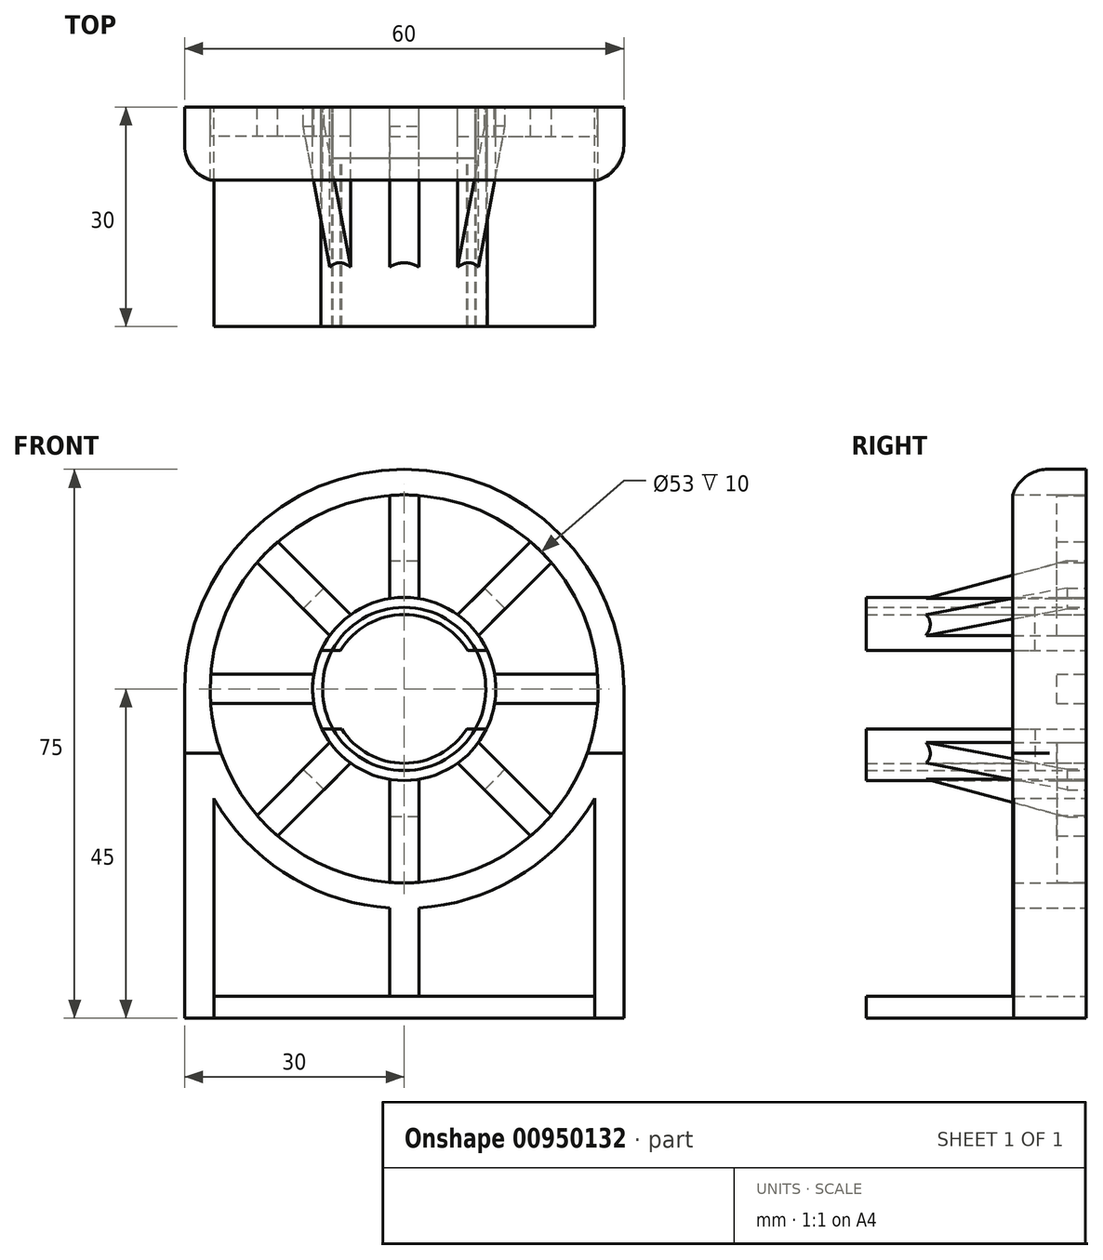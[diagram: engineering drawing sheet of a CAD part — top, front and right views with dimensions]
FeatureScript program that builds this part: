
annotation { "Feature Type Name" : "Feature", "Feature Type Description" : "" }
export const myFeature = defineFeature(function(context is Context, id is Id, definition is map)
    precondition{}
    {
        {
            var Q0;
            Q0=qCreatedBy(makeId("Front.planeOp"),FACE);
            var sketch = newSketch(context, id + "F0", { "sketchPlane" : qUnion([Q0])});
            skCircle(sketch, "E0", {"center": v(0, 0) * mm, "radius": 11.15 * mm});
            skCircle(sketch, "E1", {"center": v(0, 0) * mm, "radius": 10.15 * mm});
            skLineSegment(sketch, "E2.bottom", {"start": v(6.25, 8) * mm, "end": v(-6.25, 8) * mm});
            skLineSegment(sketch, "E2.top", {"start": v(6.25, -8) * mm, "end": v(-6.25, -8) * mm});
            skLineSegment(sketch, "E2.left", {"start": v(6.25, 8) * mm, "end": v(6.25, -8) * mm});
            skLineSegment(sketch, "E2.right", {"start": v(-6.25, 8) * mm, "end": v(-6.25, -8) * mm});
            skCircle(sketch, "E3", {"center": v(0, 0) * mm, "radius": 30 * mm});
            skCircle(sketch, "E4", {"center": v(0, 0) * mm, "radius": 26.5 * mm});
            skLineSegment(sketch, "E5", {"start": v(-30, 0) * mm, "end": v(-30, -45) * mm});
            skLineSegment(sketch, "E6", {"start": v(30, 0) * mm, "end": v(30, -45) * mm});
            skLineSegment(sketch, "E7", {"start": v(-30, -45) * mm, "end": v(30, -45) * mm});
            skLineSegment(sketch, "E8", {"start": v(-26, -45) * mm, "end": v(-26, -14.97) * mm});
            skLineSegment(sketch, "E9", {"start": v(26, -45) * mm, "end": v(26, -14.97) * mm});
            skLineSegment(sketch, "E10", {"start": v(-26, -42) * mm, "end": v(26, -42) * mm});
            skLineSegment(sketch, "E11", {"start": v(-2, -29.93) * mm, "end": v(-2, -42) * mm});
            skLineSegment(sketch, "E12", {"start": v(2, -29.93) * mm, "end": v(2, -42) * mm});
            skLineSegment(sketch, "E13", {"start": v(-8.7, 5.24) * mm, "end": v(-6.25, 5.24) * mm});
            skLineSegment(sketch, "E14", {"start": v(-6.25, 5.24) * mm, "end": v(6.25, 5.24) * mm});
            skLineSegment(sketch, "E15", {"start": v(6.25, 5.24) * mm, "end": v(8.7, 5.24) * mm});
            skLineSegment(sketch, "E16", {"start": v(8.54, -5.48) * mm, "end": v(6.25, -5.48) * mm});
            skLineSegment(sketch, "E17", {"start": v(6.25, -5.48) * mm, "end": v(-6.25, -5.48) * mm});
            skLineSegment(sketch, "E18", {"start": v(-6.25, -5.48) * mm, "end": v(-8.54, -5.48) * mm});
            skLineSegment(sketch, "E19", {"start": v(-8.7, 5.24) * mm, "end": v(-9.84, 5.24) * mm});
            skLineSegment(sketch, "E20", {"start": v(-8.54, -5.48) * mm, "end": v(-9.71, -5.48) * mm});
            skPoint(sketch, "E20.endSnap0", {"position": v(-7.4, -5.48) * mm});
            skLineSegment(sketch, "E21", {"start": v(8.54, -5.48) * mm, "end": v(9.71, -5.48) * mm});
            skLineSegment(sketch, "E22", {"start": v(8.7, 5.24) * mm, "end": v(9.84, 5.24) * mm});
            skCircle(sketch, "E23", {"center": v(0, 0) * mm, "radius": 12.5 * mm});
            skLineSegment(sketch, "E24", {"start": v(-12.34, 2) * mm, "end": v(-26.42, 2) * mm});
            skLineSegment(sketch, "E25", {"start": v(-12.34, -2) * mm, "end": v(-26.42, -2) * mm});
            skLineSegment(sketch, "E26.MirrorCS", {"start": v(12.34, 2) * mm, "end": v(26.42, 2) * mm});
            skLineSegment(sketch, "E27.MirrorCS", {"start": v(12.34, -2) * mm, "end": v(26.42, -2) * mm});
            skLineSegment(sketch, "E28", {"start": v(-2, 12.34) * mm, "end": v(-2, 26.42) * mm});
            skLineSegment(sketch, "E29", {"start": v(-2, -12.34) * mm, "end": v(-2, -26.42) * mm});
            skLineSegment(sketch, "E30.MirrorCS", {"start": v(2, 12.34) * mm, "end": v(2, 26.42) * mm});
            skLineSegment(sketch, "E31.MirrorCS", {"start": v(2, -12.34) * mm, "end": v(2, -26.42) * mm});
            skLineSegment(sketch, "E32", {"start": v(0, 0) * mm, "end": v(-18.74, 18.74) * mm});
            skLineSegment(sketch, "E33.MirrorCS", {"start": v(0, 0) * mm, "end": v(18.74, 18.74) * mm});
            skLineSegment(sketch, "E34.MirrorCS", {"start": v(0, 0) * mm, "end": v(18.74, -18.74) * mm});
            skLineSegment(sketch, "E35.MirrorCS", {"start": v(0, 0) * mm, "end": v(-18.74, -18.74) * mm});
            skLineSegment(sketch, "E36", {"start": v(-10.14, 7.31) * mm, "end": v(-20.1, 17.27) * mm});
            skLineSegment(sketch, "E37.MirrorCS", {"start": v(-7.31, 10.14) * mm, "end": v(-17.27, 20.1) * mm});
            skLineSegment(sketch, "E38.MirrorCS", {"start": v(7.31, -10.14) * mm, "end": v(17.27, -20.1) * mm});
            skLineSegment(sketch, "E39.MirrorCS", {"start": v(10.14, -7.31) * mm, "end": v(20.1, -17.27) * mm});
            skLineSegment(sketch, "E40.MirrorCS", {"start": v(10.14, 7.31) * mm, "end": v(20.1, 17.27) * mm});
            skLineSegment(sketch, "E41.MirrorCS", {"start": v(7.31, 10.14) * mm, "end": v(17.27, 20.1) * mm});
            skLineSegment(sketch, "E42.MirrorCS", {"start": v(-10.14, -7.31) * mm, "end": v(-20.1, -17.27) * mm});
            skLineSegment(sketch, "E43.MirrorCS", {"start": v(-7.31, -10.14) * mm, "end": v(-17.27, -20.1) * mm});
            skLineSegment(sketch, "E44", {"start": v(-9.84, 5.24) * mm, "end": v(-11.35, 5.24) * mm});
            skLineSegment(sketch, "E45", {"start": v(9.84, 5.24) * mm, "end": v(11.35, 5.24) * mm});
            skLineSegment(sketch, "E46", {"start": v(9.71, -5.48) * mm, "end": v(11.24, -5.48) * mm});
            skLineSegment(sketch, "E47", {"start": v(-9.71, -5.48) * mm, "end": v(-11.24, -5.48) * mm});
            skLineSegment(sketch, "E48", {"start": v(-10.96, 13.79) * mm, "end": v(-13.79, 10.96) * mm});
            skLineSegment(sketch, "E49.MirrorCS", {"start": v(10.96, 13.79) * mm, "end": v(13.79, 10.96) * mm});
            skLineSegment(sketch, "E50.MirrorCS", {"start": v(10.96, -13.79) * mm, "end": v(13.79, -10.96) * mm});
            skLineSegment(sketch, "E51.MirrorCS", {"start": v(-10.96, -13.79) * mm, "end": v(-13.79, -10.96) * mm});
            skLineSegment(sketch, "E52", {"start": v(-2, -17.5) * mm, "end": v(2, -17.5) * mm});
            skLineSegment(sketch, "E53.MirrorCS", {"start": v(-2, 17.5) * mm, "end": v(2, 17.5) * mm});
            skLineSegment(sketch, "E54.MirrorCS", {"start": v(17.5, -2) * mm, "end": v(17.5, 2) * mm});
            skLineSegment(sketch, "E55.MirrorCS", {"start": v(-17.5, 2) * mm, "end": v(-17.5, -2) * mm});
            skCircle(sketch, "E56", {"center": v(0, 0) * mm, "radius": 8.5 * mm});
            skSolve(sketch);
        }
        {
            var Q0;
            {var subQ0=sQuery(id+"F0.wireOp",EDGE,"E19");Q0=makeQuery(id+"F0.imprint","IMPRINT",FACE,{"disambiguationData":[TD([[makeQuery(id+"F0.imprint","IMPRINT",EDGE,{"derivedFrom":subQ0}),-1.0]])]});}
            var Q1;
            {var subQ4=sQuery(id+"F0.wireOp",EDGE,"E33.MirrorCS");var subQ8=sQuery(id+"F0.wireOp",EDGE,"E0");var subQ9=makeQuery(id+"F0.imprint","INTERSECT",VERTEX,{"derivedFrom":[subQ8,subQ4]});Q1=makeQuery(id+"F0.imprint","IMPRINT",FACE,{"disambiguationData":[TD([[makeQuery(id+"F0.imprint","IMPRINT",EDGE,{"disambiguationData":[TD([[subQ9,-1.0]])],"derivedFrom":subQ8}),1.0]])]});}
            var Q2;
            {var subQ0=sQuery(id+"F0.wireOp",EDGE,"E22");Q2=makeQuery(id+"F0.imprint","IMPRINT",FACE,{"disambiguationData":[TD([[makeQuery(id+"F0.imprint","IMPRINT",EDGE,{"derivedFrom":subQ0}),1.0]])]});}
            var Q3;
            {var subQ0=sQuery(id+"F0.wireOp",EDGE,"E21");Q3=makeQuery(id+"F0.imprint","IMPRINT",FACE,{"disambiguationData":[TD([[makeQuery(id+"F0.imprint","IMPRINT",EDGE,{"derivedFrom":subQ0}),-1.0]])]});}
            var Q4;
            {var subQ6=sQuery(id+"F0.wireOp",EDGE,"E35.MirrorCS");var subQ7=sQuery(id+"F0.wireOp",EDGE,"E0");var subQ8=makeQuery(id+"F0.imprint","INTERSECT",VERTEX,{"derivedFrom":[subQ7,subQ6]});Q4=makeQuery(id+"F0.imprint","IMPRINT",FACE,{"disambiguationData":[TD([[makeQuery(id+"F0.imprint","IMPRINT",EDGE,{"disambiguationData":[TD([[subQ8,-1.0]])],"derivedFrom":subQ7}),1.0]])]});}
            var Q5;
            {var subQ0=sQuery(id+"F0.wireOp",EDGE,"E20");Q5=makeQuery(id+"F0.imprint","IMPRINT",FACE,{"disambiguationData":[TD([[makeQuery(id+"F0.imprint","IMPRINT",EDGE,{"derivedFrom":subQ0}),1.0]])]});}
            extrude(context, id + "F1", {"entities" : qUnion([Q0, Q1, Q2, Q3, Q4, Q5]), "depth" : 30 * mm, "offsetDistance" : 25 * mm, "hasSecondDirection" : true, "secondDirectionOppositeDirection" : true, "secondDirectionDepth" : -7 * mm});
        }
        {
            var Q0;
            {var subQ3=sQuery(id+"F0.wireOp",EDGE,"E33.MirrorCS");var subQ5=sQuery(id+"F0.wireOp",EDGE,"E0");var subQ6=makeQuery(id+"F0.imprint","INTERSECT",VERTEX,{"derivedFrom":[subQ5,subQ3]});Q0=makeQuery(id+"F0.imprint","IMPRINT",FACE,{"disambiguationData":[TD([[makeQuery(id+"F0.imprint","IMPRINT",EDGE,{"disambiguationData":[TD([[subQ6,-1.0]])],"derivedFrom":subQ5}),-1.0]])]});}
            var Q1;
            {var subQ2=sQuery(id+"F0.wireOp",EDGE,"E44");Q1=makeQuery(id+"F0.imprint","IMPRINT",FACE,{"disambiguationData":[TD([[makeQuery(id+"F0.imprint","IMPRINT",EDGE,{"derivedFrom":subQ2}),-1.0]])]});}
            var Q2;
            {var subQ6=sQuery(id+"F0.wireOp",EDGE,"E45");Q2=makeQuery(id+"F0.imprint","IMPRINT",FACE,{"disambiguationData":[TD([[makeQuery(id+"F0.imprint","IMPRINT",EDGE,{"derivedFrom":subQ6}),1.0]])]});}
            var Q3;
            {var subQ6=sQuery(id+"F0.wireOp",EDGE,"E46");Q3=makeQuery(id+"F0.imprint","IMPRINT",FACE,{"disambiguationData":[TD([[makeQuery(id+"F0.imprint","IMPRINT",EDGE,{"derivedFrom":subQ6}),-1.0]])]});}
            var Q4;
            {var subQ4=sQuery(id+"F0.wireOp",EDGE,"E35.MirrorCS");var subQ7=sQuery(id+"F0.wireOp",EDGE,"E0");var subQ10=makeQuery(id+"F0.imprint","INTERSECT",VERTEX,{"derivedFrom":[subQ7,subQ4]});Q4=makeQuery(id+"F0.imprint","IMPRINT",FACE,{"disambiguationData":[TD([[makeQuery(id+"F0.imprint","IMPRINT",EDGE,{"disambiguationData":[TD([[subQ10,-1.0]])],"derivedFrom":subQ7}),-1.0]])]});}
            var Q5;
            {var subQ6=sQuery(id+"F0.wireOp",EDGE,"E47");Q5=makeQuery(id+"F0.imprint","IMPRINT",FACE,{"disambiguationData":[TD([[makeQuery(id+"F0.imprint","IMPRINT",EDGE,{"derivedFrom":subQ6}),1.0]])]});}
            extrude(context, id + "F2", {"entities" : qUnion([Q0, Q1, Q2, Q3, Q4, Q5]), "depth" : 30 * mm, "offsetDistance" : 25 * mm});
        }
        {
            var Q0;
            {var subQ3=sQuery(id+"F0.wireOp",EDGE,"E44");Q0=makeQuery(id+"F0.imprint","IMPRINT",FACE,{"disambiguationData":[TD([[makeQuery(id+"F0.imprint","IMPRINT",EDGE,{"derivedFrom":subQ3}),1.0]])]});}
            var Q1;
            {var subQ4=sQuery(id+"F0.wireOp",EDGE,"E45");Q1=makeQuery(id+"F0.imprint","IMPRINT",FACE,{"disambiguationData":[TD([[makeQuery(id+"F0.imprint","IMPRINT",EDGE,{"derivedFrom":subQ4}),-1.0]])]});}
            var Q2;
            {var subQ14=sQuery(id+"F0.wireOp",EDGE,"E3");var subQ18=makeQuery(id+"F0.imprint","INTERSECT",VERTEX,{"derivedFrom":[subQ14,sQuery(id+"F0.wireOp",EDGE,"E5")]});Q2=makeQuery(id+"F0.imprint","IMPRINT",FACE,{"disambiguationData":[TD([[makeQuery(id+"F0.imprint","IMPRINT",EDGE,{"disambiguationData":[TD([[subQ18,1.0]])],"derivedFrom":subQ14}),1.0]])]});}
            var Q3;
            {var subQ1=sQuery(id+"F0.wireOp",EDGE,"E5");Q3=makeQuery(id+"F0.imprint","IMPRINT",FACE,{"disambiguationData":[TD([[makeQuery(id+"F0.imprint","IMPRINT",EDGE,{"derivedFrom":subQ1}),1.0]])]});}
            var Q4;
            {var subQ4=sQuery(id+"F0.wireOp",EDGE,"E6");Q4=makeQuery(id+"F0.imprint","IMPRINT",FACE,{"disambiguationData":[TD([[makeQuery(id+"F0.imprint","IMPRINT",EDGE,{"derivedFrom":subQ4}),-1.0]])]});}
            var Q5;
            {var subQ0=sQuery(id+"F0.wireOp",EDGE,"E11");Q5=makeQuery(id+"F0.imprint","IMPRINT",FACE,{"disambiguationData":[TD([[makeQuery(id+"F0.imprint","IMPRINT",EDGE,{"derivedFrom":subQ0}),1.0]])]});}
            extrude(context, id + "F3", {"entities" : qUnion([Q0, Q1, Q2, Q3, Q4, Q5]), "depth" : 10 * mm, "offsetDistance" : 25 * mm});
        }
        {
            var Q0;
            {var subQ1=sQuery(id+"F0.wireOp",EDGE,"E8");var subQ5=sQuery(id+"F0.wireOp",EDGE,"E7");var subQ8=makeQuery(id+"F0.imprint","INTERSECT",VERTEX,{"derivedFrom":[subQ5,subQ1]});Q0=makeQuery(id+"F0.imprint","IMPRINT",FACE,{"disambiguationData":[TD([[makeQuery(id+"F0.imprint","IMPRINT",EDGE,{"disambiguationData":[TD([[subQ8,-1.0]])],"derivedFrom":subQ5}),1.0]])]});}
            extrude(context, id + "F4", {"entities" : qUnion([Q0]), "operationType" : NewBodyOperationType.ADD, "depth" : 30 * mm, "offsetDistance" : 25 * mm});
        }
        {
            var Q0;
            {var subQ0=sQuery(id+"F0.wireOp",EDGE,"E24");Q0=makeQuery(id+"F0.imprint","IMPRINT",FACE,{"disambiguationData":[TD([[makeQuery(id+"F0.imprint","IMPRINT",EDGE,{"derivedFrom":subQ0}),1.0]])]});}
            var Q1;
            {var subQ3=sQuery(id+"F0.wireOp",EDGE,"E36");Q1=makeQuery(id+"F0.imprint","IMPRINT",FACE,{"disambiguationData":[TD([[makeQuery(id+"F0.imprint","IMPRINT",EDGE,{"derivedFrom":subQ3}),-1.0]])]});}
            var Q2;
            {var subQ3=sQuery(id+"F0.wireOp",EDGE,"E37.MirrorCS");Q2=makeQuery(id+"F0.imprint","IMPRINT",FACE,{"disambiguationData":[TD([[makeQuery(id+"F0.imprint","IMPRINT",EDGE,{"derivedFrom":subQ3}),1.0]])]});}
            var Q3;
            {var subQ0=sQuery(id+"F0.wireOp",EDGE,"E28");Q3=makeQuery(id+"F0.imprint","IMPRINT",FACE,{"disambiguationData":[TD([[makeQuery(id+"F0.imprint","IMPRINT",EDGE,{"derivedFrom":subQ0}),-1.0]])]});}
            var Q4;
            {var subQ3=sQuery(id+"F0.wireOp",EDGE,"E41.MirrorCS");Q4=makeQuery(id+"F0.imprint","IMPRINT",FACE,{"disambiguationData":[TD([[makeQuery(id+"F0.imprint","IMPRINT",EDGE,{"derivedFrom":subQ3}),-1.0]])]});}
            var Q5;
            {var subQ3=sQuery(id+"F0.wireOp",EDGE,"E40.MirrorCS");Q5=makeQuery(id+"F0.imprint","IMPRINT",FACE,{"disambiguationData":[TD([[makeQuery(id+"F0.imprint","IMPRINT",EDGE,{"derivedFrom":subQ3}),1.0]])]});}
            var Q6;
            {var subQ0=sQuery(id+"F0.wireOp",EDGE,"E26.MirrorCS");Q6=makeQuery(id+"F0.imprint","IMPRINT",FACE,{"disambiguationData":[TD([[makeQuery(id+"F0.imprint","IMPRINT",EDGE,{"derivedFrom":subQ0}),-1.0]])]});}
            var Q7;
            {var subQ3=sQuery(id+"F0.wireOp",EDGE,"E39.MirrorCS");Q7=makeQuery(id+"F0.imprint","IMPRINT",FACE,{"disambiguationData":[TD([[makeQuery(id+"F0.imprint","IMPRINT",EDGE,{"derivedFrom":subQ3}),-1.0]])]});}
            var Q8;
            {var subQ3=sQuery(id+"F0.wireOp",EDGE,"E38.MirrorCS");Q8=makeQuery(id+"F0.imprint","IMPRINT",FACE,{"disambiguationData":[TD([[makeQuery(id+"F0.imprint","IMPRINT",EDGE,{"derivedFrom":subQ3}),1.0]])]});}
            var Q9;
            {var subQ0=sQuery(id+"F0.wireOp",EDGE,"E29");Q9=makeQuery(id+"F0.imprint","IMPRINT",FACE,{"disambiguationData":[TD([[makeQuery(id+"F0.imprint","IMPRINT",EDGE,{"derivedFrom":subQ0}),1.0]])]});}
            var Q10;
            {var subQ3=sQuery(id+"F0.wireOp",EDGE,"E43.MirrorCS");Q10=makeQuery(id+"F0.imprint","IMPRINT",FACE,{"disambiguationData":[TD([[makeQuery(id+"F0.imprint","IMPRINT",EDGE,{"derivedFrom":subQ3}),-1.0]])]});}
            var Q11;
            {var subQ3=sQuery(id+"F0.wireOp",EDGE,"E42.MirrorCS");Q11=makeQuery(id+"F0.imprint","IMPRINT",FACE,{"disambiguationData":[TD([[makeQuery(id+"F0.imprint","IMPRINT",EDGE,{"derivedFrom":subQ3}),1.0]])]});}
            extrude(context, id + "F5", {"entities" : qUnion([Q0, Q1, Q2, Q3, Q4, Q5, Q6, Q7, Q8, Q9, Q10, Q11]), "depth" : 4 * mm, "offsetDistance" : 25 * mm});
        }
        {
            var Q0;
            {var subQ0=sQuery(id+"F0.wireOp",EDGE,"E42.MirrorCS");var subQ1=sQuery(id+"F0.wireOp",EDGE,"E23");var subQ2=makeQuery(id+"F0.imprint","INTERSECT",VERTEX,{"derivedFrom":[subQ1,subQ0]});Q0=makeQuery(id+"F0.imprint","IMPRINT",FACE,{"disambiguationData":[TD([[makeQuery(id+"F0.imprint","IMPRINT",EDGE,{"disambiguationData":[TD([[subQ2,-1.0]])],"derivedFrom":subQ1}),-1.0]])]});}
            var Q1;
            {var subQ0=sQuery(id+"F0.wireOp",EDGE,"E43.MirrorCS");var subQ1=sQuery(id+"F0.wireOp",EDGE,"E23");var subQ2=makeQuery(id+"F0.imprint","INTERSECT",VERTEX,{"derivedFrom":[subQ1,subQ0]});Q1=makeQuery(id+"F0.imprint","IMPRINT",FACE,{"disambiguationData":[TD([[makeQuery(id+"F0.imprint","IMPRINT",EDGE,{"disambiguationData":[TD([[subQ2,1.0]])],"derivedFrom":subQ1}),-1.0]])]});}
            var Q2;
            {var subQ5=sQuery(id+"F0.wireOp",EDGE,"E52");Q2=makeQuery(id+"F0.imprint","IMPRINT",FACE,{"disambiguationData":[TD([[makeQuery(id+"F0.imprint","IMPRINT",EDGE,{"derivedFrom":subQ5}),1.0]])]});}
            var Q3;
            {var subQ0=sQuery(id+"F0.wireOp",EDGE,"E38.MirrorCS");var subQ1=sQuery(id+"F0.wireOp",EDGE,"E23");var subQ2=makeQuery(id+"F0.imprint","INTERSECT",VERTEX,{"derivedFrom":[subQ1,subQ0]});Q3=makeQuery(id+"F0.imprint","IMPRINT",FACE,{"disambiguationData":[TD([[makeQuery(id+"F0.imprint","IMPRINT",EDGE,{"disambiguationData":[TD([[subQ2,-1.0]])],"derivedFrom":subQ1}),-1.0]])]});}
            var Q4;
            {var subQ0=sQuery(id+"F0.wireOp",EDGE,"E39.MirrorCS");var subQ1=sQuery(id+"F0.wireOp",EDGE,"E23");var subQ2=makeQuery(id+"F0.imprint","INTERSECT",VERTEX,{"derivedFrom":[subQ1,subQ0]});Q4=makeQuery(id+"F0.imprint","IMPRINT",FACE,{"disambiguationData":[TD([[makeQuery(id+"F0.imprint","IMPRINT",EDGE,{"disambiguationData":[TD([[subQ2,1.0]])],"derivedFrom":subQ1}),-1.0]])]});}
            var Q5;
            {var subQ0=sQuery(id+"F0.wireOp",EDGE,"E40.MirrorCS");var subQ1=sQuery(id+"F0.wireOp",EDGE,"E23");var subQ2=makeQuery(id+"F0.imprint","INTERSECT",VERTEX,{"derivedFrom":[subQ1,subQ0]});Q5=makeQuery(id+"F0.imprint","IMPRINT",FACE,{"disambiguationData":[TD([[makeQuery(id+"F0.imprint","IMPRINT",EDGE,{"disambiguationData":[TD([[subQ2,-1.0]])],"derivedFrom":subQ1}),-1.0]])]});}
            var Q6;
            {var subQ0=sQuery(id+"F0.wireOp",EDGE,"E41.MirrorCS");var subQ1=sQuery(id+"F0.wireOp",EDGE,"E23");var subQ2=makeQuery(id+"F0.imprint","INTERSECT",VERTEX,{"derivedFrom":[subQ1,subQ0]});Q6=makeQuery(id+"F0.imprint","IMPRINT",FACE,{"disambiguationData":[TD([[makeQuery(id+"F0.imprint","IMPRINT",EDGE,{"disambiguationData":[TD([[subQ2,1.0]])],"derivedFrom":subQ1}),-1.0]])]});}
            var Q7;
            {var subQ5=sQuery(id+"F0.wireOp",EDGE,"E53.MirrorCS");Q7=makeQuery(id+"F0.imprint","IMPRINT",FACE,{"disambiguationData":[TD([[makeQuery(id+"F0.imprint","IMPRINT",EDGE,{"derivedFrom":subQ5}),-1.0]])]});}
            var Q8;
            {var subQ0=sQuery(id+"F0.wireOp",EDGE,"E37.MirrorCS");var subQ1=sQuery(id+"F0.wireOp",EDGE,"E23");var subQ2=makeQuery(id+"F0.imprint","INTERSECT",VERTEX,{"derivedFrom":[subQ1,subQ0]});Q8=makeQuery(id+"F0.imprint","IMPRINT",FACE,{"disambiguationData":[TD([[makeQuery(id+"F0.imprint","IMPRINT",EDGE,{"disambiguationData":[TD([[subQ2,-1.0]])],"derivedFrom":subQ1}),-1.0]])]});}
            var Q9;
            {var subQ0=sQuery(id+"F0.wireOp",EDGE,"E36");var subQ1=sQuery(id+"F0.wireOp",EDGE,"E23");var subQ2=makeQuery(id+"F0.imprint","INTERSECT",VERTEX,{"derivedFrom":[subQ1,subQ0]});Q9=makeQuery(id+"F0.imprint","IMPRINT",FACE,{"disambiguationData":[TD([[makeQuery(id+"F0.imprint","IMPRINT",EDGE,{"disambiguationData":[TD([[subQ2,1.0]])],"derivedFrom":subQ1}),-1.0]])]});}
            extrude(context, id + "F6", {"entities" : qUnion([Q0, Q1, Q2, Q3, Q4, Q5, Q6, Q7, Q8, Q9]), "depth" : 25 * mm, "offsetDistance" : 25 * mm});
        }
        {
            var Q0;
            Q0=makeQuery(id+"F6.opExtrude","CAP_EDGE",EDGE,{"disambiguationData":[OSD([sQuery(id+"F0.wireOp",EDGE,"E51.MirrorCS")])],"isStart":false});
            var Q1;
            Q1=makeQuery(id+"F6.opExtrude","CAP_EDGE",EDGE,{"disambiguationData":[OSD([sQuery(id+"F0.wireOp",EDGE,"E49.MirrorCS")])],"isStart":false});
            var Q2;
            Q2=makeQuery(id+"F6.opExtrude","CAP_EDGE",EDGE,{"disambiguationData":[OSD([sQuery(id+"F0.wireOp",EDGE,"E53.MirrorCS")])],"isStart":false});
            chamfer(context, id + "F7", {"entities" : qUnion([Q0, Q1, Q2]), "chamferType" : ChamferType.OFFSET_ANGLE, "width" : 6 * mm, "oppositeDirection" : true, "angle" : 75 * degree, "tangentPropagation" : true});
        }
        {
            var Q0;
            Q0=makeQuery(id+"F6.opExtrude","CAP_EDGE",EDGE,{"disambiguationData":[OSD([sQuery(id+"F0.wireOp",EDGE,"E48")])],"isStart":false});
            var Q1;
            Q1=makeQuery(id+"F6.opExtrude","CAP_EDGE",EDGE,{"disambiguationData":[OSD([sQuery(id+"F0.wireOp",EDGE,"E50.MirrorCS")])],"isStart":false});
            var Q2;
            Q2=makeQuery(id+"F6.opExtrude","CAP_EDGE",EDGE,{"disambiguationData":[OSD([sQuery(id+"F0.wireOp",EDGE,"E52")])],"isStart":false});
            chamfer(context, id + "F8", {"entities" : qUnion([Q0, Q1, Q2]), "chamferType" : ChamferType.OFFSET_ANGLE, "width" : 6 * mm, "oppositeDirection" : false, "angle" : 75 * degree, "tangentPropagation" : true});
        }
        {
            var Q0;
            Q0=makeQuery(id+"F3.opExtrude","CAP_EDGE",EDGE,{"disambiguationData":[OSD([sQuery(id+"F0.wireOp",EDGE,"E5")])],"isStart":false});
            fillet(context, id + "F9", {"entities" : qUnion([Q0]), "radius" : 5 * mm, "tangentPropagation" : true, "allowEdgeOverflow" : false});
        }
    });
